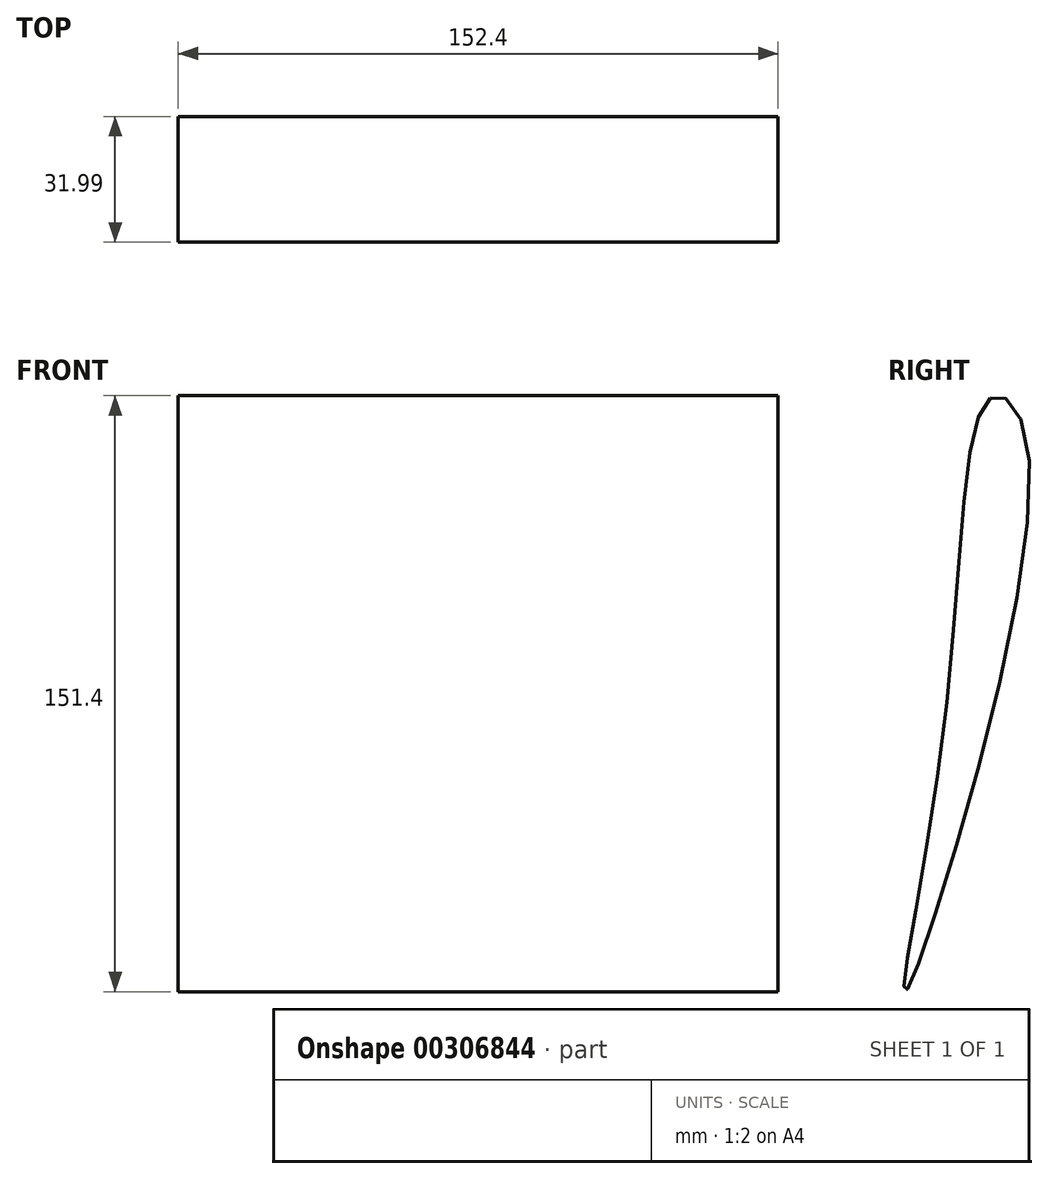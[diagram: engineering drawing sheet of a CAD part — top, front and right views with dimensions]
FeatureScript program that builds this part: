
annotation { "Feature Type Name" : "Feature", "Feature Type Description" : "" }
export const myFeature = defineFeature(function(context is Context, id is Id, definition is map)
    precondition{}
    {
        {
            var Q0;
            Q0=qCreatedBy(makeId("Right.planeOp"),FACE);
            var sketch = newSketch(context, id + "F0", { "sketchPlane" : qUnion([Q0])});
            skFitSpline(sketch, "E0", {"points": [v(19.1, 73.86) * mm, v(28.95, 59.3) * mm, v(-2.03, -76.46) * mm, v(7.39, -9.42) * mm, v(19.1, 73.86) * mm]});
            skSolve(sketch);
        }
        {
            var Q0;
            Q0=makeQuery(id+"F0.imprint","IMPRINT",FACE,{"disambiguationData":[TD([[makeQuery(id+"F0.imprint","IMPRINT",EDGE,{"derivedFrom":sQuery(id+"F0.wireOp",EDGE,"E0")}),-1.0]])]});
            extrude(context, id + "F1", {"entities" : qUnion([Q0]), "depth" : 76.2 * mm, "hasSecondDirection" : true, "secondDirectionOppositeDirection" : true, "secondDirectionDepth" : 76.2 * mm});
        }
    });
